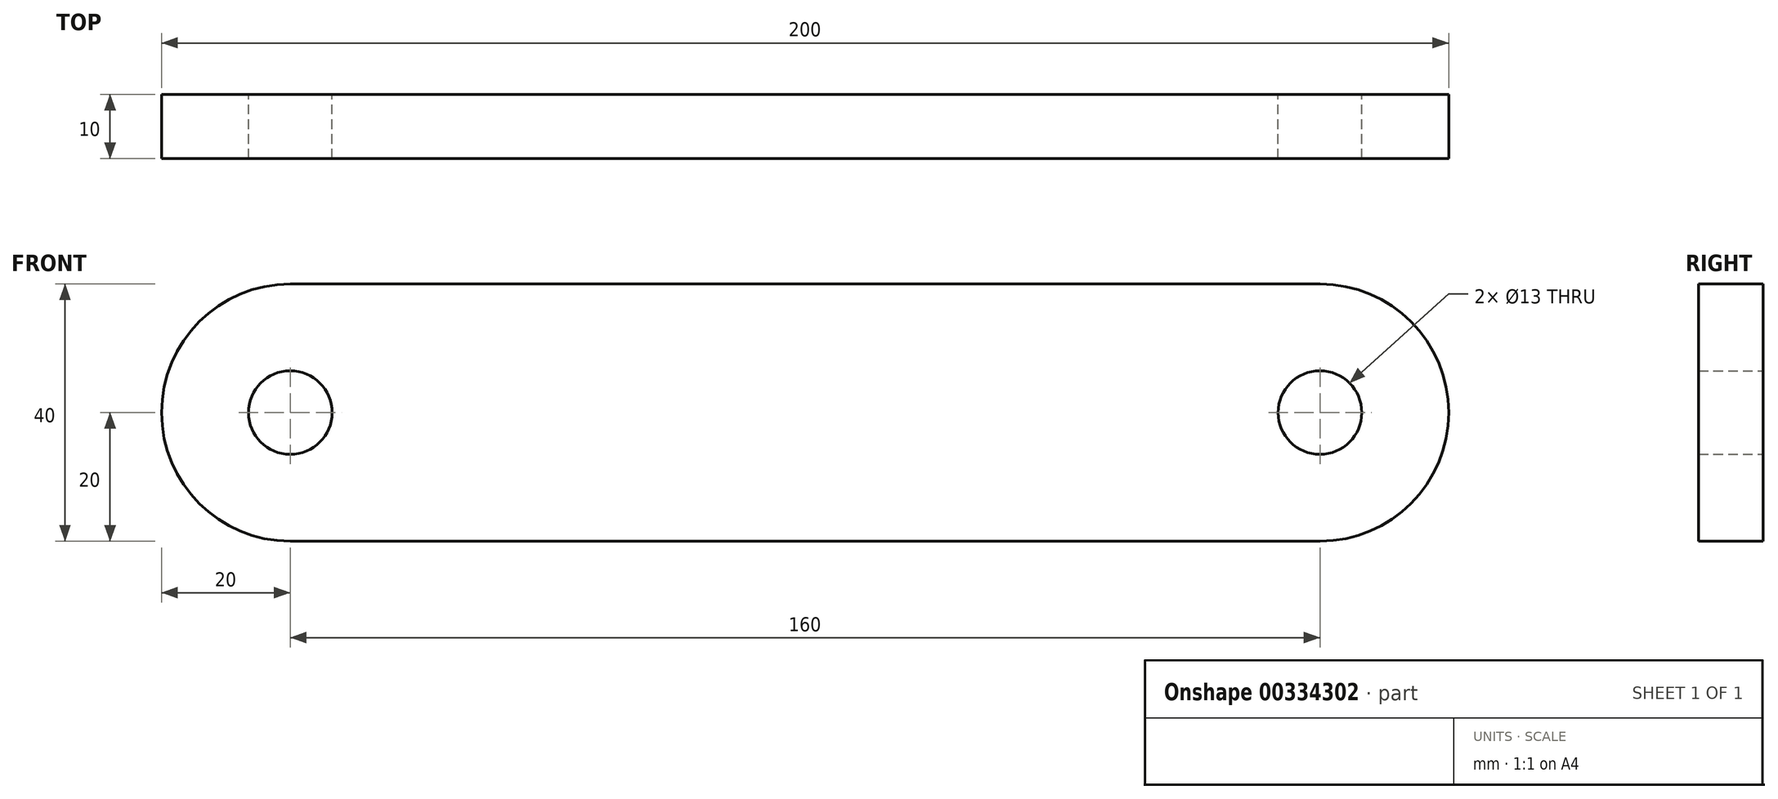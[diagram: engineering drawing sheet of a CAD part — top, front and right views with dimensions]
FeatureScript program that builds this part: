
annotation { "Feature Type Name" : "Feature", "Feature Type Description" : "" }
export const myFeature = defineFeature(function(context is Context, id is Id, definition is map)
    precondition{}
    {
        {
            var Q0;
            Q0=qCreatedBy(makeId("Front.planeOp"),FACE);
            var sketch = newSketch(context, id + "F0", { "sketchPlane" : qUnion([Q0])});
            skLineSegment(sketch, "E0", {"start": v(-80, 0) * mm, "end": v(80, 0) * mm, "construction": true});
            skLineSegment(sketch, "E1", {"start": v(0, 20) * mm, "end": v(0, -20) * mm, "construction": true});
            skCircle(sketch, "E2", {"center": v(-80, 0) * mm, "radius": 6.5 * mm});
            skCircle(sketch, "E3", {"center": v(80, 0) * mm, "radius": 6.5 * mm});
            skArc(sketch, "E4", {"start": v(80, -20) * mm, "mid": v(100, 0) * mm, "end": v(80, 20) * mm});
            skArc(sketch, "E5", {"start": v(-80, 20) * mm, "mid": v(-100, 0) * mm, "end": v(-80, -20) * mm});
            skLineSegment(sketch, "E6", {"start": v(-80, 20) * mm, "end": v(80, 20) * mm});
            skLineSegment(sketch, "E7", {"start": v(-80, -20) * mm, "end": v(80, -20) * mm});
            skSolve(sketch);
        }
        {
            var Q0;
            Q0=makeQuery(id+"F0.imprint","IMPRINT",FACE,{"disambiguationData":[TD([[makeQuery(id+"F0.imprint","IMPRINT",EDGE,{"derivedFrom":sQuery(id+"F0.wireOp",EDGE,"E2")}),-1.0]])]});
            extrude(context, id + "F1", {"entities" : qUnion([Q0]), "depth" : 10 * mm});
        }
    });
